# Revit family: Soap dispenser_CWS_Jumbo
name_source: partatom
category: Plumbing Fixtures
revit_build: Autodesk Revit Architecture 2014 (Build: 20130308_1515(x64)
units: mm (PartAtom-declared; Revit-internal decimal feet)

## types (1)
- Soap dispenser_CWS_Seifenspender Jumbo
    BIMobject category = Dispensers
    Date of publishing = 2015-09-17
    Depth = 130 mm  [stored 0.426509 ft]
    Description = Jumbo industrial dispenser for 2,000 ml = Approx. 2,000 portions of hand cleaner in a disposable bottle. Robust single-hand push-button. Exact dosing and lack of drips reduce consumption of the hand cleaner. Window for fill-level display on both sides. Housing made of impact-proof, anti-static plastic, with lock. Rounded edges ensure no risk of injury. Comes complete with fastening materials, delivery and installation.

Dispenser:
Jumbo: 411000

Abrasive soap 2.000ml:
Mild: 476000, Standard: 475000
    Design country = Switzerland
    EAN code = 4049657002292
    Edition number = 1
    Height = 332 mm  [stored 1.08924 ft]
    IFC Classification = Furniture
    Manufacturer country = Switzerland
    Manufacturer name = CWS-boco
    Manufacturer url = http://cws-boco.ie
    Material = Black Plastic - Jumbo - CWS
    Material Main = Plastic - Jumbo - CWS
    NBS Reference Code = 31-76
    NBS Reference Description = Sanitary Dispensing And Disposal Units
    Nominal height = 332
    Nominal width = 101
    Product Guid = d43e33e7-341a-447c-b8d1-5d2c305854fb
    Product SKU = 411000
    Product certification = http://www.cws-boco.de
    Product data url = http://bimobject.com
    Product family = CWS IndustryLine
    Product group = Abrasive soap dispenser
    QR code = http://bimobject.com
    UNSPSC Code = 301815
    UNSPSC name = Sanitary ware
    URL = http://cws-boco.ie
    Uniclass 1.4 Code = JN13
    Uniclass 1.4 Description = Sanitary appliances/fittings
    Uniclass 2.0 Code = PR-31-76
    Uniclass 2.0 Description = Sanitary Dispensing And Disposal Units
    Weight Net (Kg) = 0.68
    Width = 107 mm  [stored 0.35105 ft]
    Youtube clip = https://www.youtube.com

note: [stored X ft] marks values corroborated as IEEE doubles in the binary element streams (Revit-internal decimal feet)

## geometry (parser evidence)
native form markers: Sweep x4
no freeform markers — native parametric forms only
